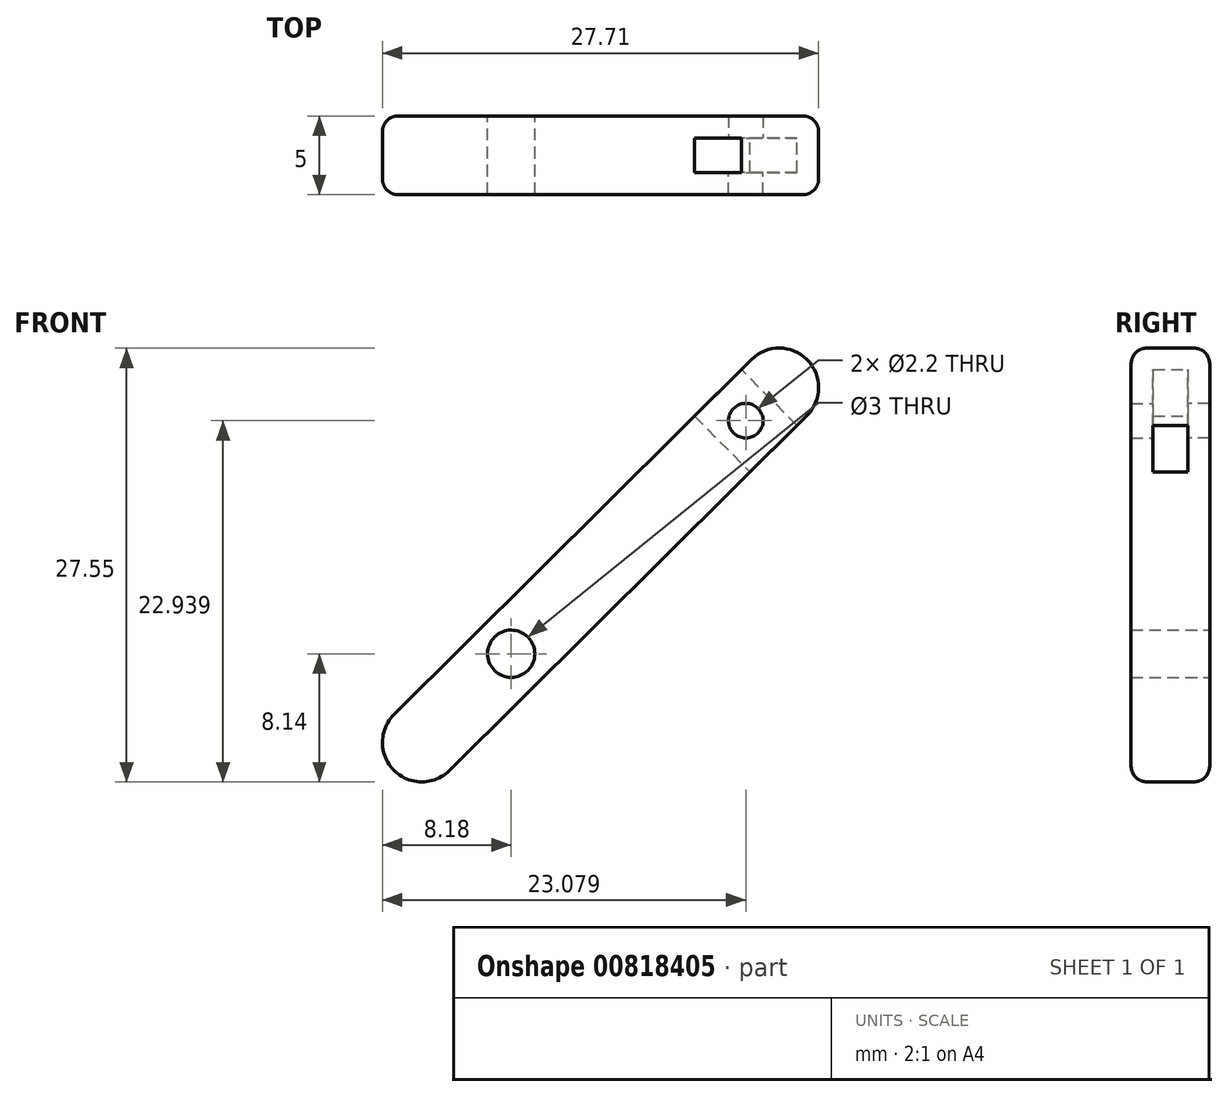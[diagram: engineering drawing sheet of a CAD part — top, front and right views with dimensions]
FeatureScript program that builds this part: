
annotation { "Feature Type Name" : "Feature", "Feature Type Description" : "" }
export const myFeature = defineFeature(function(context is Context, id is Id, definition is map)
    precondition{}
    {
        {
            var Q0;
            Q0=qCreatedBy(makeId("Front.planeOp"),FACE);
            var sketch = newSketch(context, id + "F0", { "sketchPlane" : qUnion([Q0])});
            skLineSegment(sketch, "E0.bottom", {"start": v(-3.91, -7.41) * mm, "end": v(18.79, 15.14) * mm});
            skLineSegment(sketch, "E0.top", {"start": v(-7.44, -3.86) * mm, "end": v(15.27, 18.69) * mm});
            skPoint(sketch, "E0.middle", {"position": v(5.68, 5.64) * mm});
            skArc(sketch, "E1", {"start": v(-7.44, -3.86) * mm, "mid": v(-7.45, -7.4) * mm, "end": v(-3.91, -7.41) * mm});
            skArc(sketch, "E2", {"start": v(18.79, 15.14) * mm, "mid": v(18.8, 18.67) * mm, "end": v(15.27, 18.69) * mm});
            skCircle(sketch, "E3", {"center": v(0, 0) * mm, "radius": 10.5 * mm, "construction": true});
            skCircle(sketch, "E4", {"center": v(0, 0) * mm, "radius": 1.5 * mm});
            skLineSegment(sketch, "E5", {"start": v(-5.68, -5.64) * mm, "end": v(17.03, 16.91) * mm, "construction": true});
            skLineSegment(sketch, "E6", {"start": v(-7.45, -7.4) * mm, "end": v(-7.45, -10.4) * mm, "construction": true});
            skLineSegment(sketch, "E7", {"start": v(-7.45, -10.4) * mm, "end": v(-1.45, -10.4) * mm, "construction": true});
            skLineSegment(sketch, "E8", {"start": v(0, 0) * mm, "end": v(0, -10.5) * mm, "construction": true});
            skSolve(sketch);
        }
        {
            var Q0;
            Q0=makeQuery(id+"F0.imprint","IMPRINT",FACE,{"disambiguationData":[TD([[makeQuery(id+"F0.imprint","IMPRINT",EDGE,{"derivedFrom":sQuery(id+"F0.wireOp",EDGE,"E0.bottom")}),1.0]])]});
            var Q1;
            Q1=makeQuery(id+"F0.imprint","IMPRINT",FACE,{"disambiguationData":[TD([[makeQuery(id+"F0.imprint","IMPRINT",EDGE,{"derivedFrom":sQuery(id+"F0.wireOp",EDGE,"E4")}),1.0]])]});
            extrude(context, id + "F1", {"entities" : qUnion([Q0, Q1]), "endBound" : BoundingType.SYMMETRIC, "depth" : 5 * mm, "offsetDistance" : 25 * mm});
        }
        {
            var Q0;
            Q0=makeQuery(id+"F0.imprint","IMPRINT",FACE,{"disambiguationData":[TD([[makeQuery(id+"F0.imprint","IMPRINT",EDGE,{"derivedFrom":sQuery(id+"F0.wireOp",EDGE,"E4")}),1.0]])]});
            extrude(context, id + "F2", {"entities" : qUnion([Q0]), "operationType" : NewBodyOperationType.REMOVE, "endBound" : BoundingType.SYMMETRIC, "depth" : 10 * mm, "offsetDistance" : 25 * mm});
        }
        {
            var Q0;
            Q0=makeQuery(id+"F1.opExtrude","CAP_EDGE",EDGE,{"disambiguationData":[OSD([sQuery(id+"F0.wireOp",EDGE,"E0.top")])],"isStart":false});
            var Q1;
            Q1=makeQuery(id+"F1.opExtrude","CAP_EDGE",EDGE,{"disambiguationData":[OSD([sQuery(id+"F0.wireOp",EDGE,"E0.top")])],"isStart":true});
            fillet(context, id + "F3", {"entities" : qUnion([Q0, Q1]), "radius" : 1 * mm, "tangentPropagation" : true, "allowEdgeOverflow" : false});
        }
        {
            var Q0;
            Q0=qCreatedBy(makeId("Front.planeOp"),FACE);
            var sketch = newSketch(context, id + "F4", { "sketchPlane" : qUnion([Q0])});
            skArc(sketch, "E9.0", {"start": v(-3.91, -7.41) * mm, "mid": v(-7.45, -7.4) * mm, "end": v(-7.44, -3.86) * mm});
            skLineSegment(sketch, "E10.0", {"start": v(-7.44, -3.86) * mm, "end": v(15.27, 18.69) * mm});
            skLineSegment(sketch, "E11.0", {"start": v(18.79, 15.14) * mm, "end": v(-3.91, -7.41) * mm});
            skSolve(sketch);
        }
        {
            var Q0;
            Q0=qCreatedBy(makeId("Front.planeOp"),FACE);
            var sketch = newSketch(context, id + "F5", { "sketchPlane" : qUnion([Q0])});
            skCircle(sketch, "E12.cCircle", {"center": v(14.9, 14.8) * mm, "radius": 2.1 * mm, "construction": true});
            skLineSegment(sketch, "E12.0", {"start": v(16.6, 13.08) * mm, "end": v(14.26, 12.46) * mm});
            skLineSegment(sketch, "E12.1", {"start": v(14.26, 12.46) * mm, "end": v(12.56, 14.18) * mm});
            skLineSegment(sketch, "E12.2", {"start": v(12.56, 14.18) * mm, "end": v(13.2, 16.52) * mm});
            skLineSegment(sketch, "E12.3", {"start": v(13.2, 16.52) * mm, "end": v(15.53, 17.14) * mm});
            skLineSegment(sketch, "E12.4", {"start": v(15.53, 17.14) * mm, "end": v(17.24, 15.42) * mm});
            skLineSegment(sketch, "E12.5", {"start": v(17.24, 15.42) * mm, "end": v(16.6, 13.08) * mm});
            skPoint(sketch, "E12.0.midPoint", {"position": v(15.44, 12.77) * mm});
            skLineSegment(sketch, "E13", {"start": v(14.9, 14.8) * mm, "end": v(0, 0) * mm, "construction": true});
            skLineSegment(sketch, "E14", {"start": v(11.65, 15.1) * mm, "end": v(15.17, 11.55) * mm});
            skLineSegment(sketch, "E15", {"start": v(15.17, 11.55) * mm, "end": v(18.15, 14.5) * mm});
            skLineSegment(sketch, "E16", {"start": v(18.15, 14.5) * mm, "end": v(14.63, 18.05) * mm});
            skLineSegment(sketch, "E17", {"start": v(14.63, 18.05) * mm, "end": v(11.65, 15.1) * mm});
            skSolve(sketch);
        }
        {
            var Q0;
            Q0=qSketchRegion(id+"F5",true);
            extrude(context, id + "F6", {"entities" : qUnion([Q0]), "operationType" : NewBodyOperationType.REMOVE, "endBound" : BoundingType.SYMMETRIC, "depth" : 2.2 * mm, "offsetDistance" : 25 * mm});
        }
        {
            var Q0;
            Q0=sQuery(id+"F5.wireOp",VERTEX,"E13.start");
            var Q1;
            Q1=makeQuery(id+"F1.opExtrude","SWEPT_BODY",BODY,{"disambiguationData":[OSD([sQuery(id+"F0.wireOp",EDGE,"E0.bottom"),sQuery(id+"F0.wireOp",EDGE,"E0.top"),sQuery(id+"F0.wireOp",EDGE,"E1"),sQuery(id+"F0.wireOp",EDGE,"E2")])]});
            hole(context, id + "F7", {"style" : HoleStyle.SIMPLE, "endStyle" : HoleEndStyle.THROUGH, "holeDiameter" : 2.2 * mm, "majorDiameter" : 5 * mm, "isTappedThrough" : true, "tappedDepth" : 2.3 * mm, "tapClearance" : 3, "startFromSketch" : true, "locations" : qUnion([Q0]), "scope" : qUnion([Q1])});
        }
        {
            var Q0;
            Q0=sQuery(id+"F5.wireOp",VERTEX,"E12.cCircle.center");
            var Q1;
            Q1=makeQuery(id+"F1.opExtrude","SWEPT_BODY",BODY,{"disambiguationData":[OSD([sQuery(id+"F0.wireOp",EDGE,"E0.bottom"),sQuery(id+"F0.wireOp",EDGE,"E0.top"),sQuery(id+"F0.wireOp",EDGE,"E1"),sQuery(id+"F0.wireOp",EDGE,"E2")])]});
            hole(context, id + "F8", {"style" : HoleStyle.SIMPLE, "endStyle" : HoleEndStyle.THROUGH, "oppositeDirection" : true, "holeDiameter" : 2.2 * mm, "majorDiameter" : 5 * mm, "isTappedThrough" : true, "tappedDepth" : 2.3 * mm, "tapClearance" : 3, "startFromSketch" : true, "locations" : qUnion([Q0]), "scope" : qUnion([Q1])});
        }
    });
